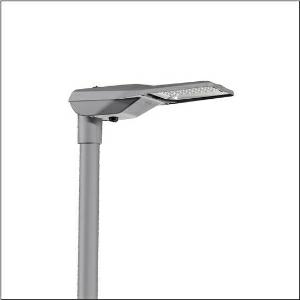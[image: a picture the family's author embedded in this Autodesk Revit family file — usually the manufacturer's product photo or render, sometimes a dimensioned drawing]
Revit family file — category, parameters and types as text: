
# Revit family: streetlight_sl_21_iq_mini___p0_8a_5xe2u31y08jb_ffd0
name_source: partatom
category: Lighting Fixtures
units: mm (PartAtom-declared; Revit-internal decimal feet)

## family parameters
Cut with Voids When Loaded = No
Host = Face
Light Source = No
Part Type = Normal
Room Calculation Point = No
Round Connector Dimension = Use Diameter
Shared = No

## types (1)
- --- (1 x LED, 11310 lm, 72.5 W, 3000K)
    Apparent Load = 73 VA
    CIE Flux Codes = 36 69 97 100 100
    Color Rendering = 70
    Color Temperature = 3000K
    Default Elevation = 1800 mm
    Description = Streetlight SL 21 iQ mini, mast luminaire, primary light control with lens, of PMMA, primary optical cover: cover, of toughened safety glass, transparent, light distribution: P0.8a, light emission: direct distribution, primary light characteristic: asymmetric, installation type: post-top, side-entry, LED, High Power LED, rated luminous flux: 11.310lm, luminous efficacy: 156lm/W, light colour: 730, colour temperature: 3000K, control gear: iQ-Street Remote, D4i with power reduction, control: pre-setting: logarithmic dimming characteristic, Street-Remote, Auto-Match, Temp-Guard, Lumen-Switch, Night-Set, Smart-Wire, Light-Fading, Desk-Remote (wireless, voltage-free reading and setting of iQ features in the workshop via application-optimized NFC function/RFID function), optimised constant luminous flux control (CLO 2.0), mains connection: 220..240V, AC, 50/60Hz, start of lifetime: 73W, end of service life: 76W, reduction: 33W, luminaire housing, of diecast aluminium, powder-coated, SITECO metallic grey (DB 702S), corrosivity category C5 high according to DIN EN ISO 12944, please order mast flange separately, inclination adjustable: 0°, 5°, 10°, 15°, sealing non-destructively replaceable, multi-level sealing system, length: 628mm, width: 235mm, height: 110mm, mast flange for spigot size: 42mm (side-entry): 5XC10008XM4, 60/48mm (side-entry/post-top): 5XC10108XM2, 76/60mm (side-entry/post-top): 5XC10108XM1, mounting height: 4..8m, Smart Interface below and above, protection rating (complete): IP66, insulation class (complete): insulation class II (safety insulation), certification: CE, ENEC, ENEC+, VDE, impact resistance: IK10, permissible operating ambient temperature for outdoor applications: -40..+50°C, standard-compliant lighting for roads and squares, packaging unit: 1 piece

Light Distribution: P0.8a
    Height = 110 mm
    Lamp = 1 x LED
    Lamp Light Flux = 11310 lm
    Lamp Power = 72.5 W
    Lamp count = 1
    Length = 625 mm
    Luminous efficacy = 156 lm/W
    Manufacturer = Siteco
    ModVariant = No
    Model = 5XE2U31Y08JB
    Number of Poles = 1
    OnlyDefault = Yes
    Power Factor = 1
    Product Name = Streetlight SL 21 iQ mini | P0.8a
    Product group = mast luminaire | pylon top
    ProductGroupID = 6100
    Protection Class = Protection class II
    Protection Degree = IP 66
    RLX_Detail_Level = 1
    RLX_Emergency_Light_Flux = 0 lm
    RLX_Emergency_Type = 0
    RLX_Emergency_Type_DB = No
    RlxData = <blob elided: 92253 chars, md5=9ca0cccc>
    Socket = socket
    Standby Power = 0 W
    System Light Flux = 11310 lm
    System Power = 73 W
    Type Comments = factory setting: luminous flux: 100 % | dim-lin: 254 | 755 mA
    Type Image = l_1003514.jpg
    URL = http://relux.com
    VarID = @adj_079839
    Voltage = 0 V
    Weight = 0.00 kg
    Width = 234 mm

## geometry (parser evidence)
native form markers: Blend x4, Sweep x10
no freeform markers — native parametric forms only
